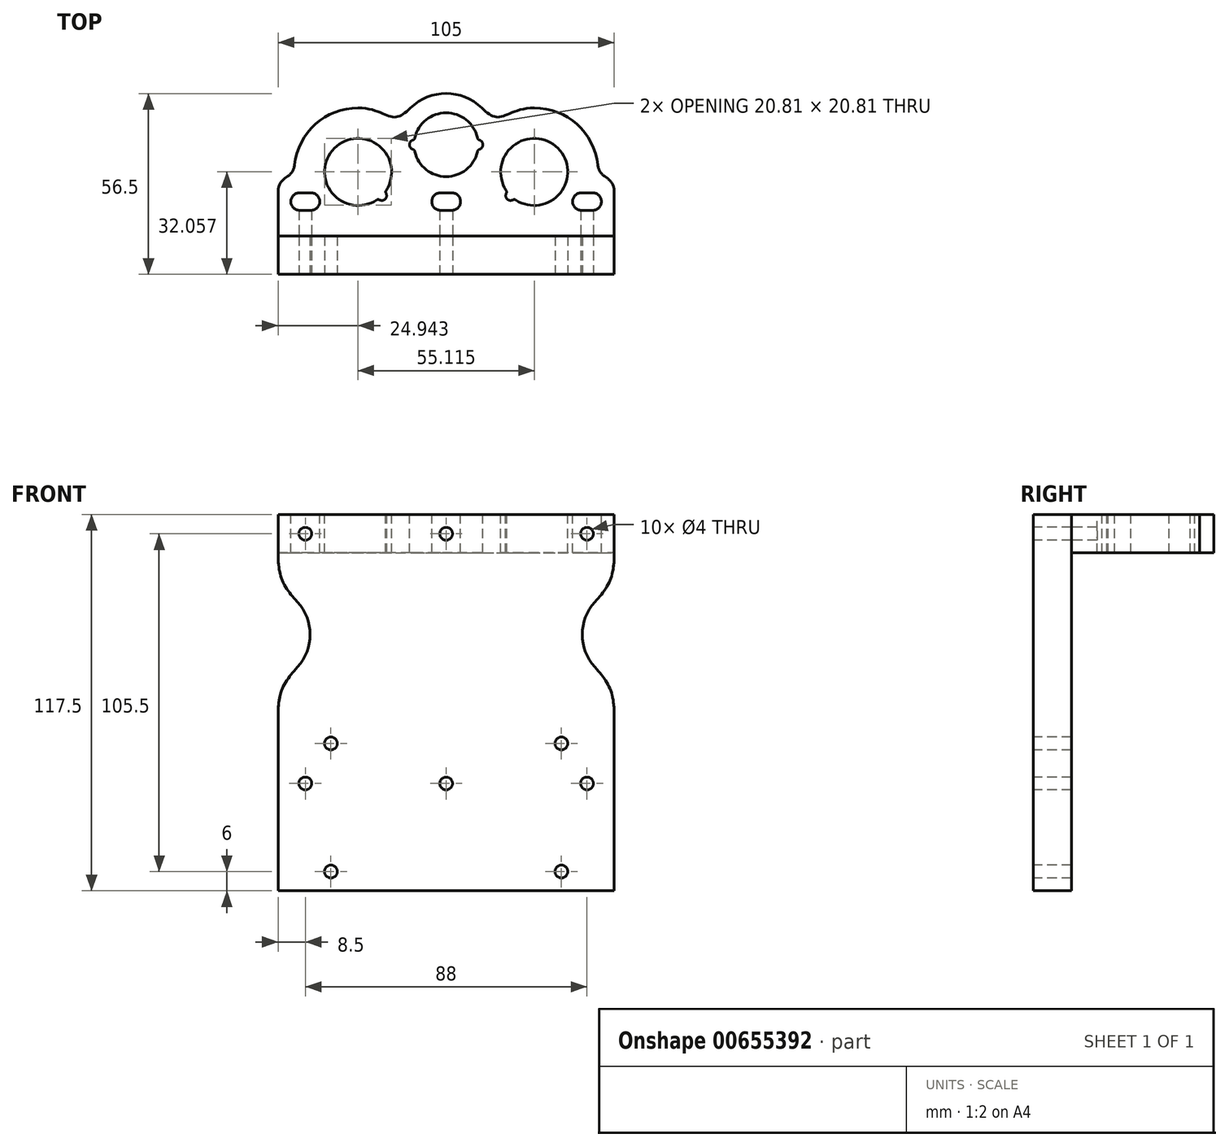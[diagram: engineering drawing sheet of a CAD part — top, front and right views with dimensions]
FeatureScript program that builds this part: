
annotation { "Feature Type Name" : "Feature", "Feature Type Description" : "" }
export const myFeature = defineFeature(function(context is Context, id is Id, definition is map)
    precondition{}
    {
        {
            var Q0;
            Q0=qCreatedBy(makeId("Front.planeOp"),FACE);
            var sketch = newSketch(context, id + "F0", { "sketchPlane" : qUnion([Q0])});
            skLineSegment(sketch, "E0.bottom", {"start": v(-52.5, 0) * mm, "end": v(52.5, 0) * mm});
            skLineSegment(sketch, "E0.top", {"start": v(-52.5, 90) * mm, "end": v(52.5, 90) * mm});
            skLineSegment(sketch, "E0.left", {"start": v(-52.5, 0) * mm, "end": v(-52.5, 90) * mm});
            skLineSegment(sketch, "E0.right", {"start": v(52.5, 0) * mm, "end": v(52.5, 90) * mm});
            skSolve(sketch);
        }
        {
            var Q0;
            Q0=qSketchRegion(id+"F0",true);
            extrude(context, id + "F1", {"entities" : qUnion([Q0]), "oppositeDirection" : true, "depth" : 12 * mm, "offsetDistance" : 25 * mm});
        }
        {
            var Q0;
            Q0=makeQuery(id+"F1.opExtrude","SWEPT_FACE",FACE,{"disambiguationData":[OSD([sQuery(id+"F0.wireOp",EDGE,"E0.top")])]});
            var sketch = newSketch(context, id + "F2", { "sketchPlane" : qUnion([Q0])});
            skLineSegment(sketch, "E1.top", {"start": v(27.5, 52) * mm, "end": v(11.12, 52) * mm, "construction": true});
            skLineSegment(sketch, "E2", {"start": v(0, 12) * mm, "end": v(0, 52) * mm, "construction": true});
            skPoint(sketch, "E3.centerSnap0", {"position": v(0, 32) * mm});
            skArc(sketch, "E4.filletArc", {"start": v(47.5, 32) * mm, "mid": v(41.64, 46.14) * mm, "end": v(27.5, 52) * mm});
            skArc(sketch, "E5.filletArc", {"start": v(-27.5, 52) * mm, "mid": v(-41.64, 46.14) * mm, "end": v(-47.5, 32) * mm});
            skArc(sketch, "E6", {"start": v(21.8, 23.22) * mm, "mid": v(34.9, 39.4) * mm, "end": v(18.72, 26.3) * mm});
            skArc(sketch, "E7.MirrorC", {"start": v(-21.8, 23.22) * mm, "mid": v(-34.9, 39.4) * mm, "end": v(-18.72, 26.3) * mm});
            skArc(sketch, "E8", {"start": v(11.12, 52) * mm, "mid": v(0, 56.5) * mm, "end": v(-11.12, 52) * mm});
            skArc(sketch, "E9", {"start": v(-9.74, 38.33) * mm, "mid": v(0, 30.53) * mm, "end": v(9.74, 38.33) * mm});
            skLineSegment(sketch, "E10", {"start": v(47.5, 12) * mm, "end": v(-47.5, 12) * mm});
            skLineSegment(sketch, "E11.bottom", {"start": v(47.5, 32) * mm, "end": v(52.5, 28.5) * mm});
            skLineSegment(sketch, "E11.top", {"start": v(47.5, 12) * mm, "end": v(52.5, 12) * mm});
            skLineSegment(sketch, "E11.right", {"start": v(52.5, 28.5) * mm, "end": v(52.5, 12) * mm});
            skLineSegment(sketch, "E12.bottom", {"start": v(42.25, 25.5) * mm, "end": v(45.75, 25.5) * mm});
            skLineSegment(sketch, "E12.top", {"start": v(42.25, 20) * mm, "end": v(45.75, 20) * mm});
            skArc(sketch, "E13", {"start": v(42.25, 25.5) * mm, "mid": v(39.5, 22.75) * mm, "end": v(42.25, 20) * mm});
            skArc(sketch, "E14", {"start": v(45.75, 20) * mm, "mid": v(48.5, 22.75) * mm, "end": v(45.75, 25.5) * mm});
            skArc(sketch, "E15.MirrorCS", {"start": v(-42.25, 25.5) * mm, "mid": v(-39.5, 22.75) * mm, "end": v(-42.25, 20) * mm});
            skLineSegment(sketch, "E16.MirrorCS", {"start": v(-42.25, 25.5) * mm, "end": v(-45.75, 25.5) * mm});
            skLineSegment(sketch, "E17.MirrorCS", {"start": v(-42.25, 20) * mm, "end": v(-45.75, 20) * mm});
            skArc(sketch, "E18.MirrorCS", {"start": v(-45.75, 20) * mm, "mid": v(-48.5, 22.75) * mm, "end": v(-45.75, 25.5) * mm});
            skLineSegment(sketch, "E19.MirrorCS", {"start": v(-47.5, 32) * mm, "end": v(-52.5, 28.5) * mm});
            skLineSegment(sketch, "E20.MirrorCS", {"start": v(-52.5, 28.5) * mm, "end": v(-52.5, 12) * mm});
            skLineSegment(sketch, "E21.MirrorCS", {"start": v(-47.5, 12) * mm, "end": v(-52.5, 12) * mm});
            skLineSegment(sketch, "E22.bottom", {"start": v(-1.75, 25.5) * mm, "end": v(1.75, 25.5) * mm});
            skLineSegment(sketch, "E22.top", {"start": v(-1.75, 20) * mm, "end": v(1.75, 20) * mm});
            skArc(sketch, "E23", {"start": v(-1.75, 25.5) * mm, "mid": v(-4.5, 22.75) * mm, "end": v(-1.75, 20) * mm});
            skArc(sketch, "E24", {"start": v(1.75, 20) * mm, "mid": v(4.5, 22.75) * mm, "end": v(1.75, 25.5) * mm});
            skLineSegment(sketch, "E25", {"start": v(-1.75, 22.75) * mm, "end": v(1.75, 22.75) * mm, "construction": true});
            skPoint(sketch, "E26", {"position": v(0, 22.75) * mm});
            skLineSegment(sketch, "E27", {"start": v(-44, 25.5) * mm, "end": v(-44, 20) * mm, "construction": true});
            skLineSegment(sketch, "E28", {"start": v(44, 20) * mm, "end": v(44, 25.5) * mm, "construction": true});
            skLineSegment(sketch, "E29.trimOffspring", {"start": v(-11.12, 52) * mm, "end": v(-27.5, 52) * mm, "construction": true});
            skFitSpline(sketch, "E30", {"points": [v(11.12, 52) * mm, v(16.56, 49.16) * mm, v(27.5, 52) * mm], "startDerivative": vector(14.38, -13.9) * mm, "endDerivative": vector(29.13, 0) * mm});
            skFitSpline(sketch, "E31.MirrorCS", {"points": [v(-11.12, 52) * mm, v(-16.56, 49.16) * mm, v(-27.5, 52) * mm], "startDerivative": vector(-14.38, -13.9) * mm, "endDerivative": vector(-29.13, 0) * mm});
            skLineSegment(sketch, "E32", {"start": v(-11.12, 52) * mm, "end": v(11.12, 52) * mm, "construction": true});
            skArc(sketch, "E33", {"start": v(-10.42, 41.93) * mm, "mid": v(-11.47, 40.5) * mm, "end": v(-10.42, 39.07) * mm});
            skArc(sketch, "E34.MirrorC", {"start": v(10.42, 41.93) * mm, "mid": v(11.47, 40.5) * mm, "end": v(10.42, 39.07) * mm});
            skArc(sketch, "E35.trimOffspring", {"start": v(9.74, 42.67) * mm, "mid": v(0, 50.48) * mm, "end": v(-9.74, 42.67) * mm});
            skPoint(sketch, "E36.visualSharp", {"position": v(-9.86, 42) * mm});
            skArc(sketch, "E36.filletArc", {"start": v(-10.42, 41.93) * mm, "mid": v(-9.98, 42.21) * mm, "end": v(-9.74, 42.67) * mm});
            skPoint(sketch, "E37.visualSharp", {"position": v(-9.86, 39) * mm});
            skArc(sketch, "E37.filletArc", {"start": v(-9.74, 38.33) * mm, "mid": v(-9.98, 38.79) * mm, "end": v(-10.42, 39.07) * mm});
            skPoint(sketch, "E38.visualSharp", {"position": v(9.86, 39) * mm});
            skArc(sketch, "E38.filletArc", {"start": v(10.42, 39.07) * mm, "mid": v(9.98, 38.79) * mm, "end": v(9.74, 38.33) * mm});
            skPoint(sketch, "E39.visualSharp", {"position": v(9.86, 42) * mm});
            skArc(sketch, "E39.filletArc", {"start": v(9.74, 42.67) * mm, "mid": v(9.98, 42.21) * mm, "end": v(10.42, 41.93) * mm});
            skArc(sketch, "E40", {"start": v(-20.79, 23.26) * mm, "mid": v(-19.03, 23.53) * mm, "end": v(-18.76, 25.29) * mm});
            skLineSegment(sketch, "E41", {"start": v(-27.5, 32) * mm, "end": v(-20.1, 24.6) * mm, "construction": true});
            skArc(sketch, "E42.MirrorCS", {"start": v(20.79, 23.26) * mm, "mid": v(19.03, 23.53) * mm, "end": v(18.76, 25.29) * mm});
            skPoint(sketch, "E43.visualSharp", {"position": v(-21.23, 23.61) * mm});
            skArc(sketch, "E43.filletArc", {"start": v(-20.79, 23.26) * mm, "mid": v(-21.3, 23.38) * mm, "end": v(-21.8, 23.22) * mm});
            skPoint(sketch, "E44.visualSharp", {"position": v(-19.11, 25.73) * mm});
            skArc(sketch, "E44.filletArc", {"start": v(-18.72, 26.3) * mm, "mid": v(-18.88, 25.8) * mm, "end": v(-18.76, 25.29) * mm});
            skPoint(sketch, "E45.visualSharp", {"position": v(19.11, 25.73) * mm});
            skArc(sketch, "E45.filletArc", {"start": v(18.76, 25.29) * mm, "mid": v(18.88, 25.8) * mm, "end": v(18.72, 26.3) * mm});
            skPoint(sketch, "E46.visualSharp", {"position": v(21.23, 23.61) * mm});
            skArc(sketch, "E46.filletArc", {"start": v(21.8, 23.22) * mm, "mid": v(21.3, 23.38) * mm, "end": v(20.79, 23.26) * mm});
            skSolve(sketch);
        }
        {
            var Q0;
            Q0=qSketchRegion(id+"F2",true);
            extrude(context, id + "F3", {"entities" : qUnion([Q0]), "oppositeDirection" : true, "depth" : 12 * mm, "offsetDistance" : 25 * mm});
        }
        {
            var Q0;
            Q0=makeQuery(id+"F3.opExtrude","SWEPT_EDGE",EDGE,{"disambiguationData":[OSD([sQuery(id+"F2.wireOp",EDGE,"E5.filletArc"),sQuery(id+"F2.wireOp",EDGE,"E19.MirrorCS")])]});
            var Q1;
            Q1=makeQuery(id+"F3.opExtrude","SWEPT_EDGE",EDGE,{"disambiguationData":[OSD([sQuery(id+"F2.wireOp",EDGE,"E19.MirrorCS"),sQuery(id+"F2.wireOp",EDGE,"E20.MirrorCS")])]});
            var Q2;
            Q2=makeQuery(id+"F3.opExtrude","SWEPT_EDGE",EDGE,{"disambiguationData":[OSD([sQuery(id+"F2.wireOp",EDGE,"E4.filletArc"),sQuery(id+"F2.wireOp",EDGE,"E11.bottom")])]});
            var Q3;
            Q3=makeQuery(id+"F3.opExtrude","SWEPT_EDGE",EDGE,{"disambiguationData":[OSD([sQuery(id+"F2.wireOp",EDGE,"E11.bottom"),sQuery(id+"F2.wireOp",EDGE,"E11.right")])]});
            fillet(context, id + "F4", {"entities" : qUnion([Q0, Q1, Q2, Q3]), "radius" : 5 * mm, "tangentPropagation" : true, "allowEdgeOverflow" : false});
        }
        {
            var Q0;
            Q0=makeQuery(id+"F1.opExtrude","CAP_FACE",FACE,{"disambiguationData":[OSD([sQuery(id+"F0.wireOp",EDGE,"E0.bottom"),sQuery(id+"F0.wireOp",EDGE,"E0.top"),sQuery(id+"F0.wireOp",EDGE,"E0.left"),sQuery(id+"F0.wireOp",EDGE,"E0.right")])],"isStart":true});
            var sketch = newSketch(context, id + "F5", { "sketchPlane" : qUnion([Q0])});
            skLineSegment(sketch, "E47.bottom", {"start": v(-52.5, 0) * mm, "end": v(52.5, 0) * mm});
            skLineSegment(sketch, "E47.top", {"start": v(-52.5, -27.5) * mm, "end": v(52.5, -27.5) * mm});
            skLineSegment(sketch, "E47.left", {"start": v(-52.5, 0) * mm, "end": v(-52.5, -27.5) * mm});
            skLineSegment(sketch, "E47.right", {"start": v(52.5, 0) * mm, "end": v(52.5, -27.5) * mm});
            skSolve(sketch);
        }
        {
            var Q0;
            Q0=qSketchRegion(id+"F5",true);
            var Q1;
            Q1=makeQuery(id+"F1.opExtrude","CAP_FACE",FACE,{"disambiguationData":[OSD([sQuery(id+"F0.wireOp",EDGE,"E0.bottom"),sQuery(id+"F0.wireOp",EDGE,"E0.top"),sQuery(id+"F0.wireOp",EDGE,"E0.left"),sQuery(id+"F0.wireOp",EDGE,"E0.right")])],"isStart":false});
            extrude(context, id + "F6", {"entities" : qUnion([Q0]), "operationType" : NewBodyOperationType.ADD, "endBound" : BoundingType.UP_TO_SURFACE, "oppositeDirection" : true, "depth" : 18 * mm, "endBoundEntityFace" : qUnion([Q1]), "offsetDistance" : 25 * mm});
        }
        {
            var Q0;
            Q0=makeQuery(id+"F1.opExtrude","CAP_FACE",FACE,{"disambiguationData":[OSD([sQuery(id+"F0.wireOp",EDGE,"E0.bottom"),sQuery(id+"F0.wireOp",EDGE,"E0.top"),sQuery(id+"F0.wireOp",EDGE,"E0.left"),sQuery(id+"F0.wireOp",EDGE,"E0.right")])],"isStart":true});
            var sketch = newSketch(context, id + "F7", { "sketchPlane" : qUnion([Q0])});
            skCircle(sketch, "E48", {"center": v(-44, 84) * mm, "radius": 2 * mm});
            skCircle(sketch, "E49", {"center": v(44, 84) * mm, "radius": 2 * mm});
            skCircle(sketch, "E50", {"center": v(0, 84) * mm, "radius": 2 * mm});
            skLineSegment(sketch, "E51", {"start": v(-52.5, 45) * mm, "end": v(52.5, 45) * mm, "construction": true});
            skCircle(sketch, "E52.MirrorC", {"center": v(44, 6) * mm, "radius": 2 * mm});
            skCircle(sketch, "E53.MirrorC", {"center": v(0, 6) * mm, "radius": 2 * mm});
            skCircle(sketch, "E54.MirrorC", {"center": v(-44, 6) * mm, "radius": 2 * mm});
            skCircle(sketch, "E55", {"center": v(-36, -21.5) * mm, "radius": 2 * mm});
            skCircle(sketch, "E56", {"center": v(36, -21.5) * mm, "radius": 2 * mm});
            skCircle(sketch, "E57.0.1.0", {"center": v(36, 18.5) * mm, "radius": 2 * mm});
            skCircle(sketch, "E57.0.1.1", {"center": v(-36, 18.5) * mm, "radius": 2 * mm});
            skLineSegment(sketch, "E57.direction1", {"start": v(-36, -21.5) * mm, "end": v(-14, -21.5) * mm, "construction": true});
            skLineSegment(sketch, "E57.direction2", {"start": v(-36, -21.5) * mm, "end": v(-36, 18.5) * mm, "construction": true});
            skSolve(sketch);
        }
        {
            var Q0;
            Q0=qSketchRegion(id+"F7",true);
            extrude(context, id + "F8", {"entities" : qUnion([Q0]), "operationType" : NewBodyOperationType.REMOVE, "oppositeDirection" : true, "depth" : 25 * mm, "offsetDistance" : 25 * mm});
        }
        {
            var Q0;
            Q0=makeQuery(id+"F6.boolean.opBoolean","MERGE",FACE,{"derivedFrom":[makeQuery(id+"F1.opExtrude","CAP_FACE",FACE,{"disambiguationData":[OSD([sQuery(id+"F0.wireOp",EDGE,"E0.bottom"),sQuery(id+"F0.wireOp",EDGE,"E0.top"),sQuery(id+"F0.wireOp",EDGE,"E0.left"),sQuery(id+"F0.wireOp",EDGE,"E0.right")])],"isStart":true}),makeQuery(id+"F6.opExtrude","CAP_FACE",FACE,{"disambiguationData":[OSD([sQuery(id+"F5.wireOp",EDGE,"E47.bottom"),sQuery(id+"F5.wireOp",EDGE,"E47.top"),sQuery(id+"F5.wireOp",EDGE,"E47.left"),sQuery(id+"F5.wireOp",EDGE,"E47.right")])],"isStart":true})]});
            var sketch = newSketch(context, id + "F9", { "sketchPlane" : qUnion([Q0])});
            skCircle(sketch, "E58", {"center": v(-57.5, 52.5) * mm, "radius": 15 * mm});
            skLineSegment(sketch, "E59", {"start": v(-52.5, 27) * mm, "end": v(52.5, 27) * mm, "construction": true});
            skLineSegment(sketch, "E60", {"start": v(0, 27) * mm, "end": v(0, 90) * mm, "construction": true});
            skCircle(sketch, "E61.MirrorC", {"center": v(57.5, 52.5) * mm, "radius": 15 * mm});
            skSolve(sketch);
        }
        {
            var Q0;
            Q0=qSketchRegion(id+"F9",true);
            extrude(context, id + "F10", {"entities" : qUnion([Q0]), "operationType" : NewBodyOperationType.REMOVE, "oppositeDirection" : true, "depth" : 25 * mm, "offsetDistance" : 25 * mm});
        }
        {
            var Q0;
            Q0=makeQuery(id+"F10.boolean.opBoolean","INTERSECT",EDGE,{"disambiguationData":[OD(0.0)],"derivedFrom":[makeQuery(id+"F6.boolean.opBoolean","MERGE",FACE,{"derivedFrom":[makeQuery(id+"F1.opExtrude","SWEPT_FACE",FACE,{"disambiguationData":[OSD([sQuery(id+"F0.wireOp",EDGE,"E0.left")])]}),makeQuery(id+"F6.opExtrude","SWEPT_FACE",FACE,{"disambiguationData":[OSD([sQuery(id+"F5.wireOp",EDGE,"E47.left")])]})]}),makeQuery(id+"F10.opExtrude","SWEPT_FACE",FACE,{"disambiguationData":[OSD([sQuery(id+"F9.wireOp",EDGE,"E58")])]})]});
            var Q1;
            Q1=makeQuery(id+"F10.boolean.opBoolean","INTERSECT",EDGE,{"disambiguationData":[OD(1.0)],"derivedFrom":[makeQuery(id+"F6.boolean.opBoolean","MERGE",FACE,{"derivedFrom":[makeQuery(id+"F1.opExtrude","SWEPT_FACE",FACE,{"disambiguationData":[OSD([sQuery(id+"F0.wireOp",EDGE,"E0.left")])]}),makeQuery(id+"F6.opExtrude","SWEPT_FACE",FACE,{"disambiguationData":[OSD([sQuery(id+"F5.wireOp",EDGE,"E47.left")])]})]}),makeQuery(id+"F10.opExtrude","SWEPT_FACE",FACE,{"disambiguationData":[OSD([sQuery(id+"F9.wireOp",EDGE,"E58")])]})]});
            var Q2;
            Q2=makeQuery(id+"F10.boolean.opBoolean","INTERSECT",EDGE,{"disambiguationData":[OD(0.0)],"derivedFrom":[makeQuery(id+"F6.boolean.opBoolean","MERGE",FACE,{"derivedFrom":[makeQuery(id+"F1.opExtrude","SWEPT_FACE",FACE,{"disambiguationData":[OSD([sQuery(id+"F0.wireOp",EDGE,"E0.right")])]}),makeQuery(id+"F6.opExtrude","SWEPT_FACE",FACE,{"disambiguationData":[OSD([sQuery(id+"F5.wireOp",EDGE,"E47.right")])]})]}),makeQuery(id+"F10.opExtrude","SWEPT_FACE",FACE,{"disambiguationData":[OSD([sQuery(id+"F9.wireOp",EDGE,"E61.MirrorC")])]})]});
            var Q3;
            Q3=makeQuery(id+"F10.boolean.opBoolean","INTERSECT",EDGE,{"disambiguationData":[OD(1.0)],"derivedFrom":[makeQuery(id+"F6.boolean.opBoolean","MERGE",FACE,{"derivedFrom":[makeQuery(id+"F1.opExtrude","SWEPT_FACE",FACE,{"disambiguationData":[OSD([sQuery(id+"F0.wireOp",EDGE,"E0.right")])]}),makeQuery(id+"F6.opExtrude","SWEPT_FACE",FACE,{"disambiguationData":[OSD([sQuery(id+"F5.wireOp",EDGE,"E47.right")])]})]}),makeQuery(id+"F10.opExtrude","SWEPT_FACE",FACE,{"disambiguationData":[OSD([sQuery(id+"F9.wireOp",EDGE,"E61.MirrorC")])]})]});
            fillet(context, id + "F11", {"entities" : qUnion([Q0, Q1, Q2, Q3]), "radius" : 23 * mm, "tangentPropagation" : true, "rho" : 0.6, "crossSection" : FilletCrossSection.CONIC, "allowEdgeOverflow" : false});
        }
    });
